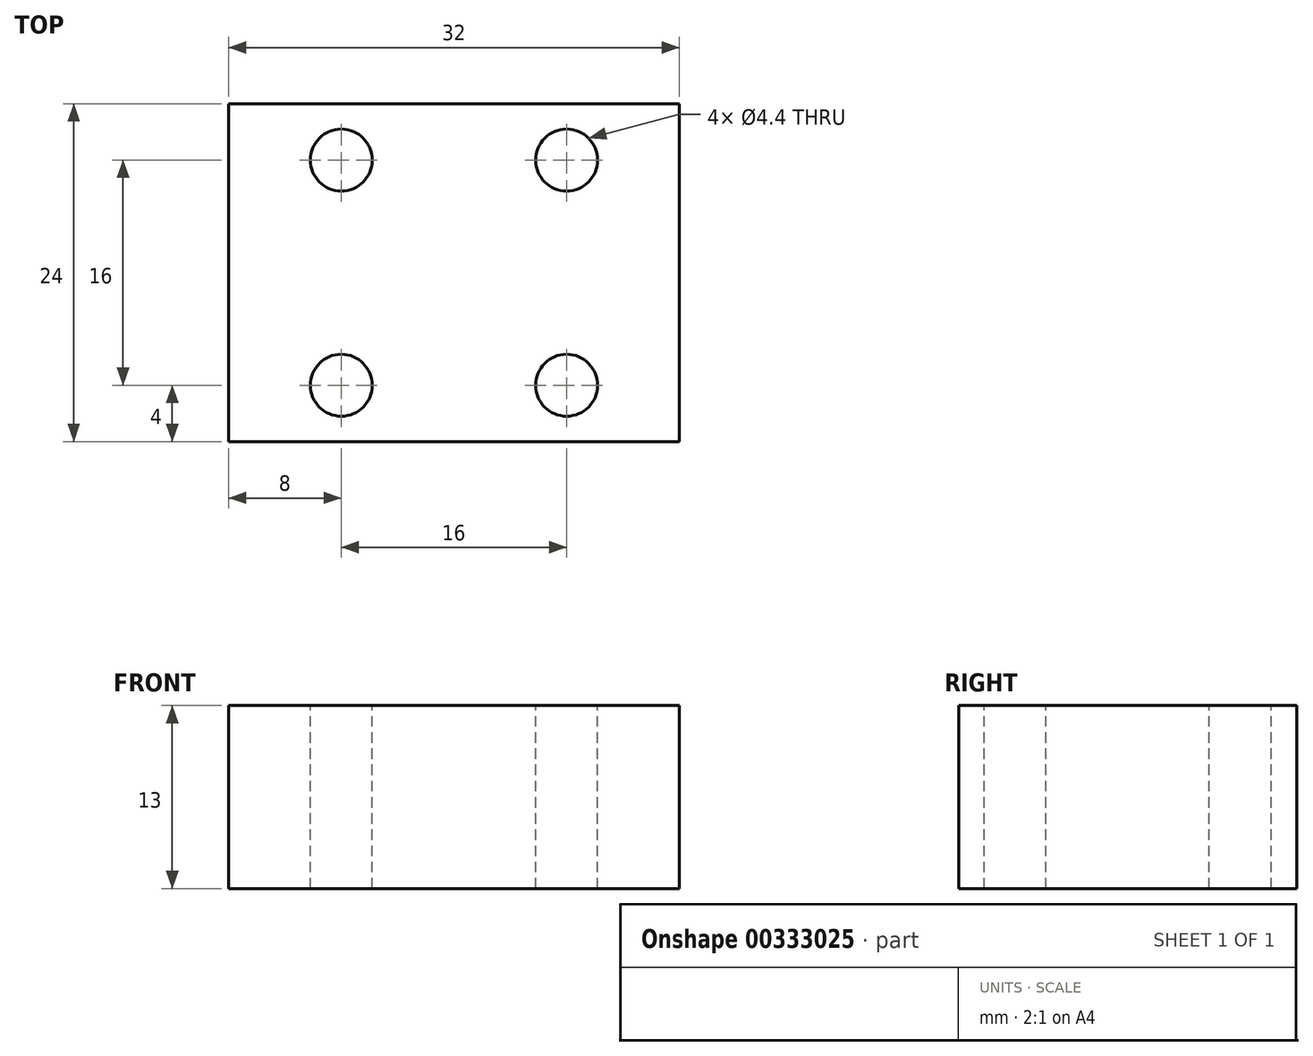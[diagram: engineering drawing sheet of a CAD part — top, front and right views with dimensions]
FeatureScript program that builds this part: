
annotation { "Feature Type Name" : "Feature", "Feature Type Description" : "" }
export const myFeature = defineFeature(function(context is Context, id is Id, definition is map)
    precondition{}
    {
        {
            var Q0;
            Q0=qCreatedBy(makeId("Top.planeOp"),FACE);
            var sketch = newSketch(context, id + "F0", { "sketchPlane" : qUnion([Q0])});
            skLineSegment(sketch, "E0.bottom", {"start": v(-16, 11.5) * mm, "end": v(16, 11.5) * mm});
            skLineSegment(sketch, "E0.top", {"start": v(-16, -12.5) * mm, "end": v(16, -12.5) * mm});
            skLineSegment(sketch, "E0.left", {"start": v(-16, 11.5) * mm, "end": v(-16, -12.5) * mm});
            skLineSegment(sketch, "E0.right", {"start": v(16, 11.5) * mm, "end": v(16, -12.5) * mm});
            skSolve(sketch);
        }
        {
            var Q0;
            Q0 = qSketchRegion(id + "F0", true);
            var Q1;
            Q1 = qSketchRegion(id + "F2", true);
            extrude(context, id + "F1", {"entities" : qUnion([Q0, Q1]), "depth" : 13 * mm});
        }
        {
            var Q0;
            Q0=makeQuery(id+"F1.opExtrude","SWEPT_FACE",FACE,{"disambiguationData":[OSD([sQuery(id+"F0.wireOp",EDGE,"E0.top")])]});
            var sketch = newSketch(context, id + "F2", { "sketchPlane" : qUnion([Q0])});
            skSolve(sketch);
        }
        {
            var Q0;
            Q0=makeQuery(id+"F1.opExtrude","CAP_FACE",FACE,{"disambiguationData":[OSD([sQuery(id+"F0.wireOp",EDGE,"E0.bottom"),sQuery(id+"F0.wireOp",EDGE,"E0.top"),sQuery(id+"F0.wireOp",EDGE,"E0.left"),sQuery(id+"F0.wireOp",EDGE,"E0.right")])],"isStart":false});
            var sketch = newSketch(context, id + "F3", { "sketchPlane" : qUnion([Q0])});
            skPoint(sketch, "E1", {"position": v(8, -8.5) * mm});
            skPoint(sketch, "E2", {"position": v(8, 7.5) * mm});
            skPoint(sketch, "E3", {"position": v(-8, 7.5) * mm});
            skPoint(sketch, "E4", {"position": v(-8, -8.5) * mm});
            skSolve(sketch);
        }
        {
            var Q0;
            Q0=sQuery(id+"F3.wireOp",VERTEX,"E3");
            var Q1;
            Q1=sQuery(id+"F3.wireOp",VERTEX,"E2");
            var Q2;
            Q2=sQuery(id+"F3.wireOp",VERTEX,"E1");
            var Q3;
            Q3=sQuery(id+"F3.wireOp",VERTEX,"E4");
            var Q4;
            Q4=makeQuery(id+"F1.opExtrude","SWEPT_BODY",BODY,{"disambiguationData":[OSD([sQuery(id+"F0.wireOp",EDGE,"E0.bottom"),sQuery(id+"F0.wireOp",EDGE,"E0.top"),sQuery(id+"F0.wireOp",EDGE,"E0.left"),sQuery(id+"F0.wireOp",EDGE,"E0.right")])]});
            hole(context, id + "F4", {"style" : HoleStyle.SIMPLE, "endStyle" : HoleEndStyle.THROUGH, "standardTappedOrClearance" : lookupTablePath({ "standard" : "ISO", "fit" : "Normal", "size" : "M4", "type" : "Clearance" }), "standardBlindInLast" : lookupTablePath({ "fit" : "Standard", "standard" : "ISO", "size" : "M4", "type" : "Clearance" }), "holeDiameter" : 4.4 * mm, "tappedDepth" : 12 * mm, "tapClearance" : 3, "locations" : qUnion([Q0, Q1, Q2, Q3]), "scope" : qUnion([Q4])});
        }
    });
